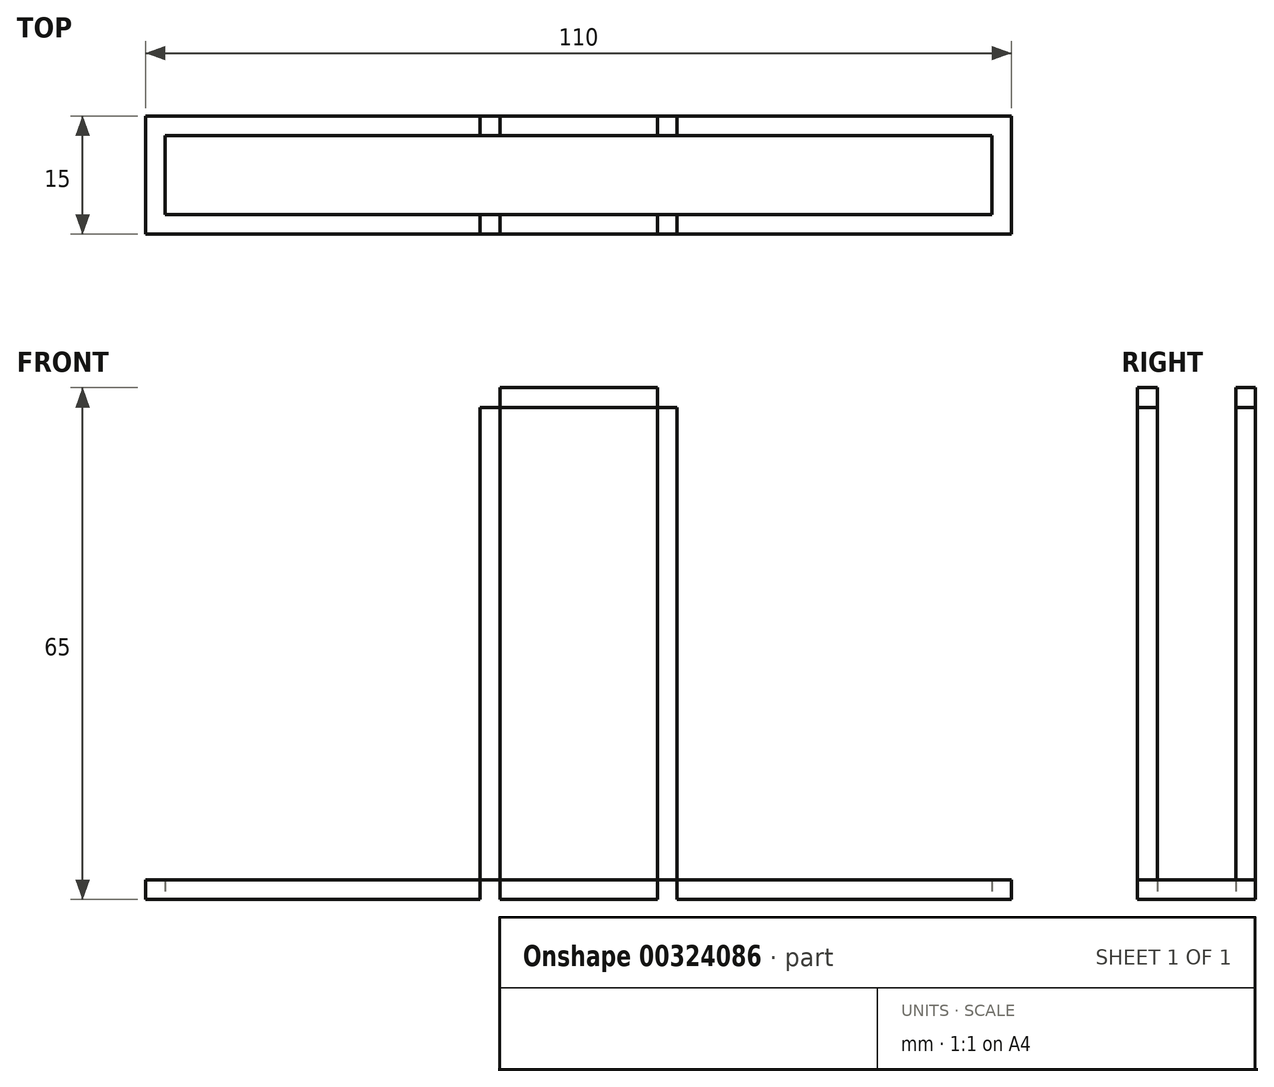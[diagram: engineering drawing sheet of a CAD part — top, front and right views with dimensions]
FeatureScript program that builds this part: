
annotation { "Feature Type Name" : "Feature", "Feature Type Description" : "" }
export const myFeature = defineFeature(function(context is Context, id is Id, definition is map)
    precondition{}
    {
        {
            var Q0;
            Q0=qCreatedBy(makeId("Front.planeOp"),FACE);
            var sketch = newSketch(context, id + "F0", { "sketchPlane" : qUnion([Q0])});
            skLineSegment(sketch, "E0.bottom", {"start": v(-55, 0) * mm, "end": v(55, 0) * mm});
            skLineSegment(sketch, "E0.top", {"start": v(-55, 2.5) * mm, "end": v(55, 2.5) * mm});
            skLineSegment(sketch, "E0.left", {"start": v(-55, 0) * mm, "end": v(-55, 2.5) * mm});
            skLineSegment(sketch, "E0.right", {"start": v(55, 0) * mm, "end": v(55, 2.5) * mm});
            skLineSegment(sketch, "E1.bottom", {"start": v(-12.5, 0) * mm, "end": v(-10, 0) * mm});
            skLineSegment(sketch, "E1.top", {"start": v(-12.5, 65) * mm, "end": v(-10, 65) * mm});
            skLineSegment(sketch, "E1.left", {"start": v(-12.5, 0) * mm, "end": v(-12.5, 65) * mm});
            skLineSegment(sketch, "E1.right", {"start": v(-10, 0) * mm, "end": v(-10, 65) * mm});
            skLineSegment(sketch, "E2.bottom", {"start": v(-12.5, 65) * mm, "end": v(12.5, 65) * mm});
            skLineSegment(sketch, "E2.top", {"start": v(-12.5, 62.5) * mm, "end": v(12.5, 62.5) * mm});
            skLineSegment(sketch, "E2.left", {"start": v(-12.5, 65) * mm, "end": v(-12.5, 62.5) * mm});
            skLineSegment(sketch, "E2.right", {"start": v(12.5, 65) * mm, "end": v(12.5, 62.5) * mm});
            skLineSegment(sketch, "E3.bottom", {"start": v(12.5, 65) * mm, "end": v(10, 65) * mm});
            skLineSegment(sketch, "E3.top", {"start": v(12.5, 0) * mm, "end": v(10, 0) * mm});
            skLineSegment(sketch, "E3.left", {"start": v(12.5, 65) * mm, "end": v(12.5, 0) * mm});
            skLineSegment(sketch, "E3.right", {"start": v(10, 65) * mm, "end": v(10, 0) * mm});
            skLineSegment(sketch, "E4", {"start": v(-52.5, 0) * mm, "end": v(-52.5, 2.5) * mm});
            skLineSegment(sketch, "E5", {"start": v(52.5, 0) * mm, "end": v(52.5, 2.5) * mm});
            skSolve(sketch);
        }
        {
            var Q0;
            {var subQ5=sQuery(id+"F0.wireOp",EDGE,"E2.left");Q0=makeQuery(id+"F0.imprint","IMPRINT",FACE,{"disambiguationData":[TD([[makeQuery(id+"F0.imprint","IMPRINT",EDGE,{"derivedFrom":subQ5}),1.0]])]});}
            var Q1;
            {var subQ0=sQuery(id+"F0.wireOp",EDGE,"E2.bottom");var subQ1=sQuery(id+"F0.wireOp",EDGE,"E1.right");var subQ2=makeQuery(id+"F0.imprint","INTERSECT",VERTEX,{"derivedFrom":[subQ1,subQ0]});Q1=makeQuery(id+"F0.imprint","IMPRINT",FACE,{"disambiguationData":[TD([[makeQuery(id+"F0.imprint","IMPRINT",EDGE,{"disambiguationData":[TD([[subQ2,1.0]])],"derivedFrom":subQ1}),-1.0]])]});}
            var Q2;
            {var subQ5=sQuery(id+"F0.wireOp",EDGE,"E3.bottom");Q2=makeQuery(id+"F0.imprint","IMPRINT",FACE,{"disambiguationData":[TD([[makeQuery(id+"F0.imprint","IMPRINT",EDGE,{"derivedFrom":subQ5}),1.0]])]});}
            var Q3;
            {var subQ0=sQuery(id+"F0.wireOp",EDGE,"E1.left");var subQ1=sQuery(id+"F0.wireOp",EDGE,"E0.top");var subQ2=makeQuery(id+"F0.imprint","INTERSECT",VERTEX,{"derivedFrom":[subQ1,subQ0]});Q3=makeQuery(id+"F0.imprint","IMPRINT",FACE,{"disambiguationData":[TD([[makeQuery(id+"F0.imprint","IMPRINT",EDGE,{"disambiguationData":[TD([[subQ2,-1.0]])],"derivedFrom":subQ1}),1.0]])]});}
            var Q4;
            {var subQ0=sQuery(id+"F0.wireOp",EDGE,"E3.left");var subQ1=sQuery(id+"F0.wireOp",EDGE,"E0.top");var subQ2=makeQuery(id+"F0.imprint","INTERSECT",VERTEX,{"derivedFrom":[subQ1,subQ0]});Q4=makeQuery(id+"F0.imprint","IMPRINT",FACE,{"disambiguationData":[TD([[makeQuery(id+"F0.imprint","IMPRINT",EDGE,{"disambiguationData":[TD([[subQ2,1.0]])],"derivedFrom":subQ1}),1.0]])]});}
            var Q5;
            {var subQ0=sQuery(id+"F0.wireOp",EDGE,"E1.right");var subQ5=sQuery(id+"F0.wireOp",EDGE,"E0.top");var subQ6=makeQuery(id+"F0.imprint","INTERSECT",VERTEX,{"derivedFrom":[subQ5,subQ0]});Q5=makeQuery(id+"F0.imprint","IMPRINT",FACE,{"disambiguationData":[TD([[makeQuery(id+"F0.imprint","IMPRINT",EDGE,{"disambiguationData":[TD([[subQ6,-1.0]])],"derivedFrom":subQ5}),-1.0]])]});}
            var Q6;
            {var subQ3=sQuery(id+"F0.wireOp",EDGE,"E4");Q6=makeQuery(id+"F0.imprint","IMPRINT",FACE,{"disambiguationData":[TD([[makeQuery(id+"F0.imprint","IMPRINT",EDGE,{"derivedFrom":subQ3}),-1.0]])]});}
            var Q7;
            {var subQ3=sQuery(id+"F0.wireOp",EDGE,"E5");Q7=makeQuery(id+"F0.imprint","IMPRINT",FACE,{"disambiguationData":[TD([[makeQuery(id+"F0.imprint","IMPRINT",EDGE,{"derivedFrom":subQ3}),1.0]])]});}
            var Q8;
            {var subQ5=sQuery(id+"F0.wireOp",EDGE,"E3.top");Q8=makeQuery(id+"F0.imprint","IMPRINT",FACE,{"disambiguationData":[TD([[makeQuery(id+"F0.imprint","IMPRINT",EDGE,{"derivedFrom":subQ5}),-1.0]])]});}
            var Q9;
            {var subQ0=sQuery(id+"F0.wireOp",EDGE,"E0.right");Q9=makeQuery(id+"F0.imprint","IMPRINT",FACE,{"disambiguationData":[TD([[makeQuery(id+"F0.imprint","IMPRINT",EDGE,{"derivedFrom":subQ0}),1.0]])]});}
            var Q10;
            {var subQ5=sQuery(id+"F0.wireOp",EDGE,"E1.bottom");Q10=makeQuery(id+"F0.imprint","IMPRINT",FACE,{"disambiguationData":[TD([[makeQuery(id+"F0.imprint","IMPRINT",EDGE,{"derivedFrom":subQ5}),1.0]])]});}
            var Q11;
            {var subQ0=sQuery(id+"F0.wireOp",EDGE,"E0.left");Q11=makeQuery(id+"F0.imprint","IMPRINT",FACE,{"disambiguationData":[TD([[makeQuery(id+"F0.imprint","IMPRINT",EDGE,{"derivedFrom":subQ0}),-1.0]])]});}
            extrude(context, id + "F1", {"entities" : qUnion([Q0, Q1, Q2, Q3, Q4, Q5, Q6, Q7, Q8, Q9, Q10, Q11]), "depth" : 15 * mm, "offsetDistance" : 25 * mm});
        }
        {
            var Q0;
            Q0=qCreatedBy(makeId("Top.planeOp"),FACE);
            var sketch = newSketch(context, id + "F2", { "sketchPlane" : qUnion([Q0])});
            skLineSegment(sketch, "E6.bottom", {"start": v(-52.5, -2.5) * mm, "end": v(-12.5, -2.5) * mm});
            skLineSegment(sketch, "E6.top", {"start": v(-52.5, -12.5) * mm, "end": v(-12.5, -12.5) * mm});
            skLineSegment(sketch, "E6.left", {"start": v(-52.5, -2.5) * mm, "end": v(-52.5, -12.5) * mm});
            skLineSegment(sketch, "E6.right", {"start": v(-12.5, -2.5) * mm, "end": v(-12.5, -12.5) * mm});
            skLineSegment(sketch, "E7.bottom", {"start": v(-10, -2.5) * mm, "end": v(10, -2.5) * mm});
            skLineSegment(sketch, "E7.top", {"start": v(-10, -12.5) * mm, "end": v(10, -12.5) * mm});
            skLineSegment(sketch, "E7.left", {"start": v(-10, -2.5) * mm, "end": v(-10, -12.5) * mm});
            skLineSegment(sketch, "E7.right", {"start": v(10, -2.5) * mm, "end": v(10, -12.5) * mm});
            skLineSegment(sketch, "E8.bottom", {"start": v(12.5, -2.5) * mm, "end": v(52.5, -2.5) * mm});
            skLineSegment(sketch, "E8.top", {"start": v(12.5, -12.5) * mm, "end": v(52.5, -12.5) * mm});
            skLineSegment(sketch, "E8.left", {"start": v(12.5, -2.5) * mm, "end": v(12.5, -12.5) * mm});
            skLineSegment(sketch, "E8.right", {"start": v(52.5, -2.5) * mm, "end": v(52.5, -12.5) * mm});
            skSolve(sketch);
        }
        {
            var Q0;
            Q0=makeQuery(id+"F2.imprint","IMPRINT",FACE,{"disambiguationData":[TD([[makeQuery(id+"F2.imprint","IMPRINT",EDGE,{"derivedFrom":sQuery(id+"F2.wireOp",EDGE,"E7.bottom")}),-1.0]])]});
            var Q1;
            Q1=makeQuery(id+"F2.imprint","IMPRINT",FACE,{"disambiguationData":[TD([[makeQuery(id+"F2.imprint","IMPRINT",EDGE,{"derivedFrom":sQuery(id+"F2.wireOp",EDGE,"E8.bottom")}),-1.0]])]});
            var Q2;
            Q2=makeQuery(id+"F2.imprint","IMPRINT",FACE,{"disambiguationData":[TD([[makeQuery(id+"F2.imprint","IMPRINT",EDGE,{"derivedFrom":sQuery(id+"F2.wireOp",EDGE,"E6.bottom")}),-1.0]])]});
            extrude(context, id + "F3", {"entities" : qUnion([Q0, Q1, Q2]), "operationType" : NewBodyOperationType.REMOVE, "depth" : 70 * mm, "offsetDistance" : 25 * mm});
        }
        {
            var Q0;
            Q0=qCreatedBy(makeId("Right.planeOp"),FACE);
            var sketch = newSketch(context, id + "F4", { "sketchPlane" : qUnion([Q0])});
            skLineSegment(sketch, "E9.bottom", {"start": v(-2.5, 2.5) * mm, "end": v(-12.5, 2.5) * mm});
            skLineSegment(sketch, "E9.top", {"start": v(-2.5, 62.5) * mm, "end": v(-12.5, 62.5) * mm});
            skLineSegment(sketch, "E9.left", {"start": v(-2.5, 2.5) * mm, "end": v(-2.5, 62.5) * mm});
            skLineSegment(sketch, "E9.right", {"start": v(-12.5, 2.5) * mm, "end": v(-12.5, 62.5) * mm});
            skSolve(sketch);
        }
        {
            var Q0;
            Q0=makeQuery(id+"F4.imprint","IMPRINT",FACE,{"disambiguationData":[TD([[makeQuery(id+"F4.imprint","IMPRINT",EDGE,{"derivedFrom":sQuery(id+"F4.wireOp",EDGE,"E9.bottom")}),-1.0]])]});
            extrude(context, id + "F5", {"entities" : qUnion([Q0]), "operationType" : NewBodyOperationType.REMOVE, "oppositeDirection" : true, "depth" : 25 * mm, "offsetDistance" : 25 * mm, "hasSecondDirection" : true, "secondDirectionOppositeDirection" : false, "secondDirectionDepth" : 25 * mm});
        }
    });
